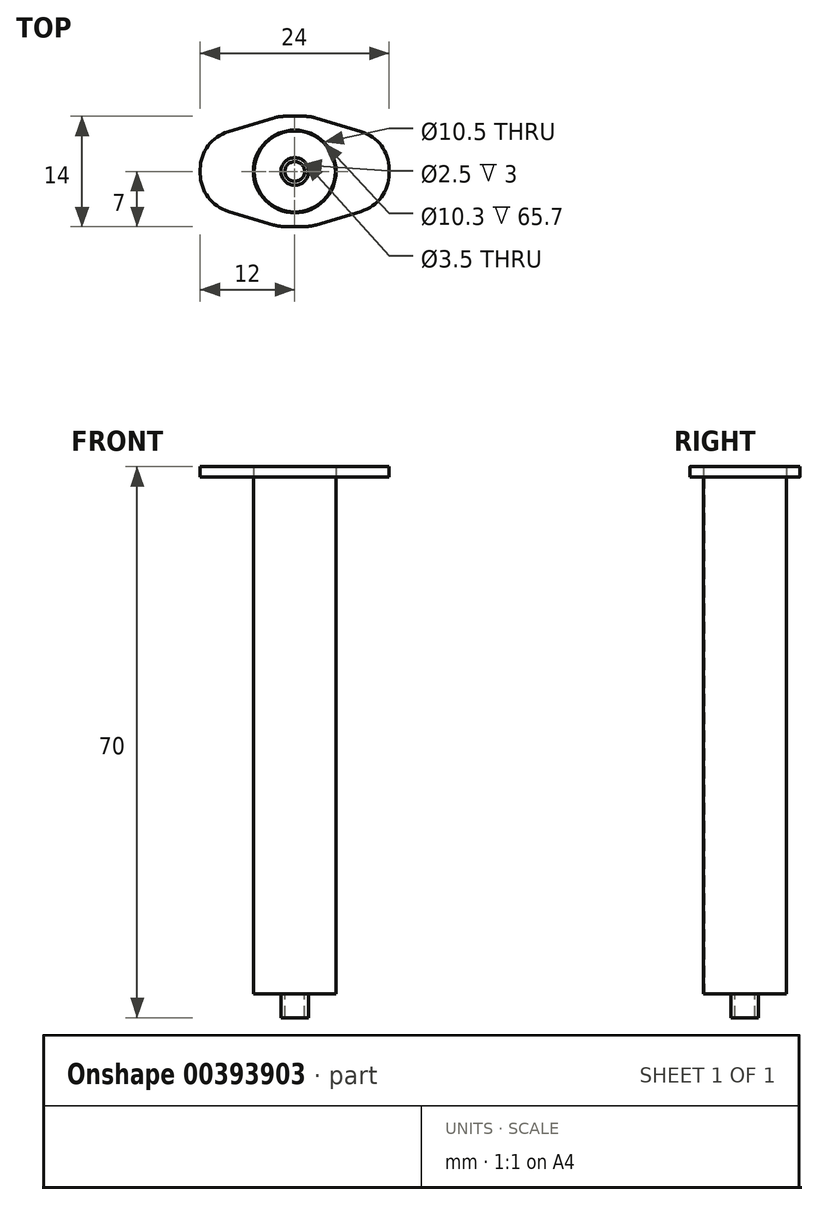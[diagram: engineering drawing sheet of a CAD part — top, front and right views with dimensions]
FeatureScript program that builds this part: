
annotation { "Feature Type Name" : "Feature", "Feature Type Description" : "" }
export const myFeature = defineFeature(function(context is Context, id is Id, definition is map)
    precondition{}
    {
        {
            var Q0;
            Q0=qCreatedBy(makeId("Top.planeOp"),FACE);
            var sketch = newSketch(context, id + "F0", { "sketchPlane" : qUnion([Q0])});
            skCircle(sketch, "E0", {"center": v(0, 0) * mm, "radius": 5.25 * mm});
            skCircle(sketch, "E1", {"center": v(0, 0) * mm, "radius": 5.15 * mm});
            skSolve(sketch);
        }
        {
            var Q0;
            Q0=makeQuery(id+"F0.imprint","IMPRINT",FACE,{"disambiguationData":[TD([[makeQuery(id+"F0.imprint","IMPRINT",EDGE,{"derivedFrom":sQuery(id+"F0.wireOp",EDGE,"E0")}),1.0]])]});
            extrude(context, id + "F1", {"entities" : qUnion([Q0]), "depth" : 65.7 * mm, "offsetDistance" : 25 * mm});
        }
        {
            var Q0;
            Q0=makeQuery(id+"F1.opExtrude","CAP_FACE",FACE,{"disambiguationData":[OSD([sQuery(id+"F0.wireOp",EDGE,"E0"),sQuery(id+"F0.wireOp",EDGE,"E1")])],"isStart":false});
            var sketch = newSketch(context, id + "F2", { "sketchPlane" : qUnion([Q0])});
            skCircle(sketch, "E2", {"center": v(0, 0) * mm, "radius": 5.15 * mm});
            skLineSegment(sketch, "E3.bottom", {"start": v(12, 7) * mm, "end": v(-12, 7) * mm});
            skLineSegment(sketch, "E3.top", {"start": v(12, -7) * mm, "end": v(-12, -7) * mm});
            skLineSegment(sketch, "E3.left", {"start": v(12, 7) * mm, "end": v(12, -7) * mm});
            skLineSegment(sketch, "E3.right", {"start": v(-12, 7) * mm, "end": v(-12, -7) * mm});
            skSolve(sketch);
        }
        {
            var Q0;
            Q0=makeQuery(id+"F2.imprint","IMPRINT",FACE,{"disambiguationData":[TD([[makeQuery(id+"F2.imprint","IMPRINT",EDGE,{"derivedFrom":sQuery(id+"F2.wireOp",EDGE,"E3.bottom")}),1.0]])]});
            extrude(context, id + "F3", {"entities" : qUnion([Q0]), "depth" : 1.3 * mm, "offsetDistance" : 25 * mm});
        }
        {
            var Q0;
            Q0=makeQuery(id+"F3.opExtrude","SWEPT_EDGE",EDGE,{"disambiguationData":[OSD([sQuery(id+"F2.wireOp",EDGE,"E3.bottom"),sQuery(id+"F2.wireOp",EDGE,"E3.right")])]});
            var Q1;
            Q1=makeQuery(id+"F3.opExtrude","SWEPT_EDGE",EDGE,{"disambiguationData":[OSD([sQuery(id+"F2.wireOp",EDGE,"E3.bottom"),sQuery(id+"F2.wireOp",EDGE,"E3.left")])]});
            var Q2;
            Q2=makeQuery(id+"F3.opExtrude","SWEPT_EDGE",EDGE,{"disambiguationData":[OSD([sQuery(id+"F2.wireOp",EDGE,"E3.top"),sQuery(id+"F2.wireOp",EDGE,"E3.left")])]});
            var Q3;
            Q3=makeQuery(id+"F3.opExtrude","SWEPT_EDGE",EDGE,{"disambiguationData":[OSD([sQuery(id+"F2.wireOp",EDGE,"E3.top"),sQuery(id+"F2.wireOp",EDGE,"E3.right")])]});
            chamfer(context, id + "F4", {"entities" : qUnion([Q0, Q1, Q2, Q3]), "chamferType" : ChamferType.TWO_OFFSETS, "width1" : 3 * mm, "oppositeDirection" : false, "width2" : 10 * mm, "tangentPropagation" : true});
        }
        {
            var Q0;
            {var subQ0=sQuery(id+"F2.wireOp",EDGE,"E3.right");Q0=makeQuery(id+"F4.opChamfer","BLEND_EDGE",EDGE,{"blendedFrom":[makeQuery(id+"F3.opExtrude","SWEPT_EDGE",EDGE,{"disambiguationData":[OSD([sQuery(id+"F2.wireOp",EDGE,"E3.top"),subQ0])]}),makeQuery(id+"F3.opExtrude","SWEPT_FACE",FACE,{"disambiguationData":[OSD([subQ0])]})],"blendedInto":[makeQuery(id+"F3.opExtrude","SWEPT_FACE",FACE,{"disambiguationData":[OSD([subQ0])]})]});}
            var Q1;
            {var subQ0=sQuery(id+"F2.wireOp",EDGE,"E3.top");Q1=makeQuery(id+"F4.opChamfer","BLEND_EDGE",EDGE,{"blendedFrom":[makeQuery(id+"F3.opExtrude","SWEPT_EDGE",EDGE,{"disambiguationData":[OSD([subQ0,sQuery(id+"F2.wireOp",EDGE,"E3.right")])]}),makeQuery(id+"F3.opExtrude","SWEPT_FACE",FACE,{"disambiguationData":[OSD([subQ0])]})],"blendedInto":[makeQuery(id+"F3.opExtrude","SWEPT_FACE",FACE,{"disambiguationData":[OSD([subQ0])]})]});}
            var Q2;
            {var subQ0=sQuery(id+"F2.wireOp",EDGE,"E3.top");Q2=makeQuery(id+"F4.opChamfer","BLEND_EDGE",EDGE,{"blendedFrom":[makeQuery(id+"F3.opExtrude","SWEPT_EDGE",EDGE,{"disambiguationData":[OSD([subQ0,sQuery(id+"F2.wireOp",EDGE,"E3.left")])]}),makeQuery(id+"F3.opExtrude","SWEPT_FACE",FACE,{"disambiguationData":[OSD([subQ0])]})],"blendedInto":[makeQuery(id+"F3.opExtrude","SWEPT_FACE",FACE,{"disambiguationData":[OSD([subQ0])]})]});}
            var Q3;
            {var subQ0=sQuery(id+"F2.wireOp",EDGE,"E3.left");Q3=makeQuery(id+"F4.opChamfer","BLEND_EDGE",EDGE,{"blendedFrom":[makeQuery(id+"F3.opExtrude","SWEPT_EDGE",EDGE,{"disambiguationData":[OSD([sQuery(id+"F2.wireOp",EDGE,"E3.top"),subQ0])]}),makeQuery(id+"F3.opExtrude","SWEPT_FACE",FACE,{"disambiguationData":[OSD([subQ0])]})],"blendedInto":[makeQuery(id+"F3.opExtrude","SWEPT_FACE",FACE,{"disambiguationData":[OSD([subQ0])]})]});}
            var Q4;
            {var subQ0=sQuery(id+"F2.wireOp",EDGE,"E3.left");Q4=makeQuery(id+"F4.opChamfer","BLEND_EDGE",EDGE,{"blendedFrom":[makeQuery(id+"F3.opExtrude","SWEPT_EDGE",EDGE,{"disambiguationData":[OSD([sQuery(id+"F2.wireOp",EDGE,"E3.bottom"),subQ0])]}),makeQuery(id+"F3.opExtrude","SWEPT_FACE",FACE,{"disambiguationData":[OSD([subQ0])]})],"blendedInto":[makeQuery(id+"F3.opExtrude","SWEPT_FACE",FACE,{"disambiguationData":[OSD([subQ0])]})]});}
            var Q5;
            {var subQ0=sQuery(id+"F2.wireOp",EDGE,"E3.bottom");Q5=makeQuery(id+"F4.opChamfer","BLEND_EDGE",EDGE,{"blendedFrom":[makeQuery(id+"F3.opExtrude","SWEPT_EDGE",EDGE,{"disambiguationData":[OSD([subQ0,sQuery(id+"F2.wireOp",EDGE,"E3.left")])]}),makeQuery(id+"F3.opExtrude","SWEPT_FACE",FACE,{"disambiguationData":[OSD([subQ0])]})],"blendedInto":[makeQuery(id+"F3.opExtrude","SWEPT_FACE",FACE,{"disambiguationData":[OSD([subQ0])]})]});}
            var Q6;
            {var subQ0=sQuery(id+"F2.wireOp",EDGE,"E3.bottom");Q6=makeQuery(id+"F4.opChamfer","BLEND_EDGE",EDGE,{"blendedFrom":[makeQuery(id+"F3.opExtrude","SWEPT_EDGE",EDGE,{"disambiguationData":[OSD([subQ0,sQuery(id+"F2.wireOp",EDGE,"E3.right")])]}),makeQuery(id+"F3.opExtrude","SWEPT_FACE",FACE,{"disambiguationData":[OSD([subQ0])]})],"blendedInto":[makeQuery(id+"F3.opExtrude","SWEPT_FACE",FACE,{"disambiguationData":[OSD([subQ0])]})]});}
            var Q7;
            {var subQ0=sQuery(id+"F2.wireOp",EDGE,"E3.right");Q7=makeQuery(id+"F4.opChamfer","BLEND_EDGE",EDGE,{"blendedFrom":[makeQuery(id+"F3.opExtrude","SWEPT_EDGE",EDGE,{"disambiguationData":[OSD([sQuery(id+"F2.wireOp",EDGE,"E3.bottom"),subQ0])]}),makeQuery(id+"F3.opExtrude","SWEPT_FACE",FACE,{"disambiguationData":[OSD([subQ0])]})],"blendedInto":[makeQuery(id+"F3.opExtrude","SWEPT_FACE",FACE,{"disambiguationData":[OSD([subQ0])]})]});}
            fillet(context, id + "F5", {"entities" : qUnion([Q0, Q1, Q2, Q3, Q4, Q5, Q6, Q7]), "radius" : 5 * mm, "tangentPropagation" : true, "allowEdgeOverflow" : false});
        }
        {
            var Q0;
            Q0=makeQuery(id+"F1.opExtrude","CAP_FACE",FACE,{"disambiguationData":[OSD([sQuery(id+"F0.wireOp",EDGE,"E0"),sQuery(id+"F0.wireOp",EDGE,"E1")])],"isStart":true});
            var sketch = newSketch(context, id + "F6", { "sketchPlane" : qUnion([Q0])});
            skCircle(sketch, "E4", {"center": v(0, 0) * mm, "radius": 5.25 * mm});
            skCircle(sketch, "E5", {"center": v(0, 0) * mm, "radius": 1.75 * mm});
            skSolve(sketch);
        }
        {
            var Q0;
            Q0=makeQuery(id+"F6.imprint","IMPRINT",FACE,{"disambiguationData":[TD([[makeQuery(id+"F6.imprint","IMPRINT",EDGE,{"derivedFrom":sQuery(id+"F6.wireOp",EDGE,"E5")}),-1.0]])]});
            extrude(context, id + "F7", {"entities" : qUnion([Q0]), "oppositeDirection" : true, "depth" : 0.1 * mm, "offsetDistance" : 25 * mm});
        }
        {
            var Q0;
            Q0=makeQuery(id+"F7.opExtrude","CAP_FACE",FACE,{"disambiguationData":[OSD([sQuery(id+"F0.wireOp",EDGE,"E1"),sQuery(id+"F6.wireOp",EDGE,"E5")])],"isStart":true});
            var sketch = newSketch(context, id + "F8", { "sketchPlane" : qUnion([Q0])});
            skCircle(sketch, "E6", {"center": v(0, 0) * mm, "radius": 1.75 * mm});
            skCircle(sketch, "E7", {"center": v(0, 0) * mm, "radius": 1.25 * mm});
            skSolve(sketch);
        }
        {
            var Q0;
            Q0=makeQuery(id+"F8.imprint","IMPRINT",FACE,{"disambiguationData":[TD([[makeQuery(id+"F8.imprint","IMPRINT",EDGE,{"derivedFrom":sQuery(id+"F8.wireOp",EDGE,"E6")}),1.0]])]});
            extrude(context, id + "F9", {"entities" : qUnion([Q0]), "depth" : 3 * mm, "offsetDistance" : 25 * mm});
        }
    });
